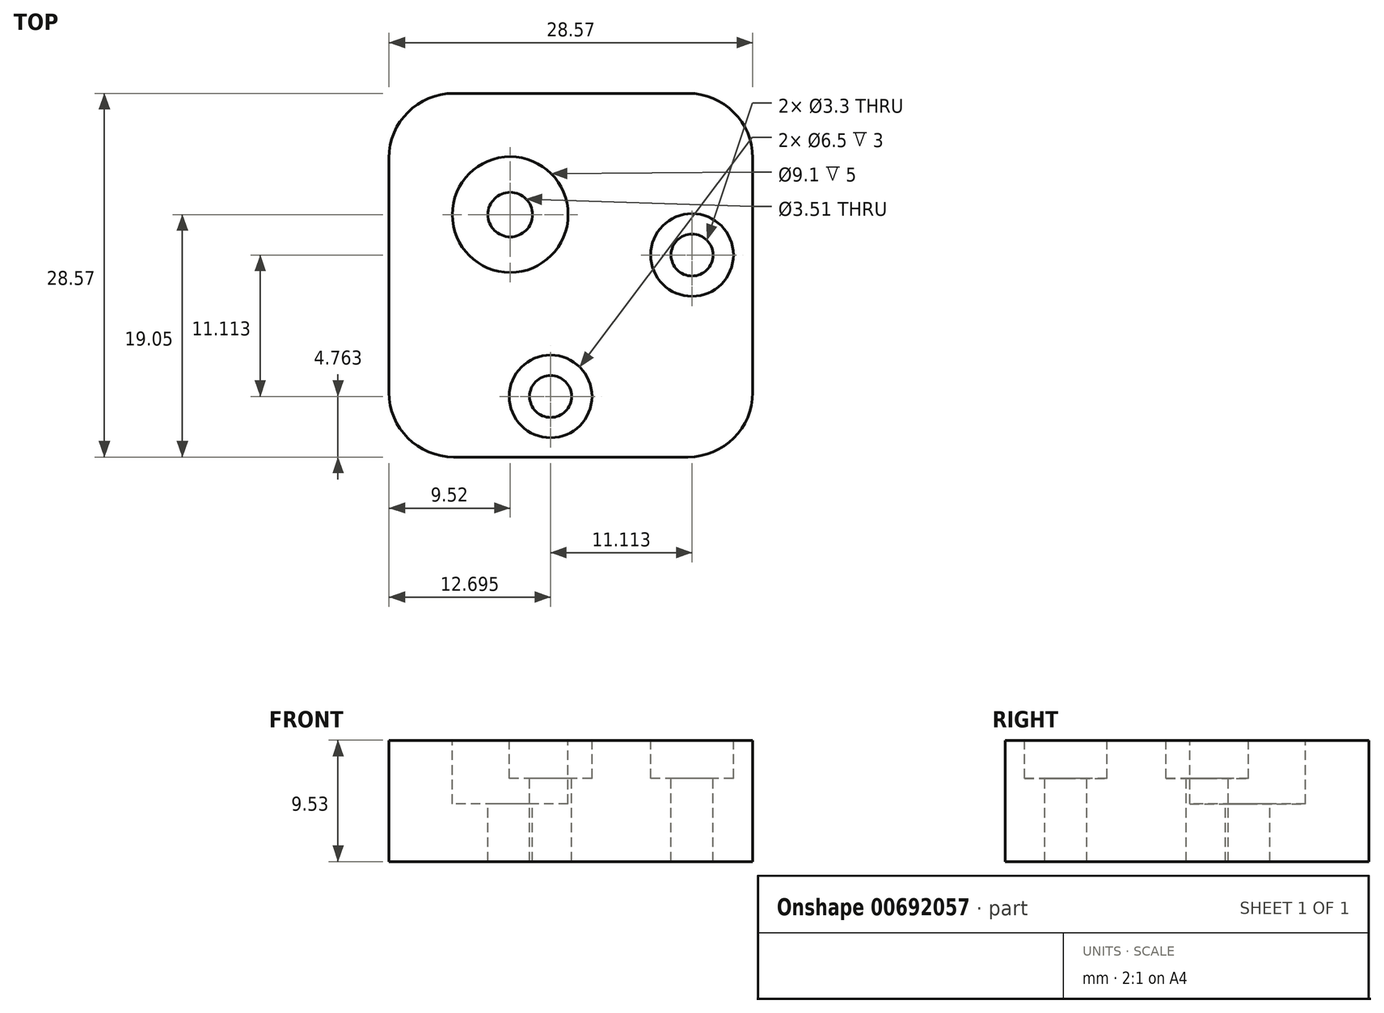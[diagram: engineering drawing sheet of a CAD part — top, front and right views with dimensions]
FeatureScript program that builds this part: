
annotation { "Feature Type Name" : "Feature", "Feature Type Description" : "" }
export const myFeature = defineFeature(function(context is Context, id is Id, definition is map)
    precondition{}
    {
        {
            var Q0;
            Q0=qCreatedBy(makeId("Top.planeOp"),FACE);
            var sketch = newSketch(context, id + "F0", { "sketchPlane" : qUnion([Q0])});
            skLineSegment(sketch, "E0.bottom", {"start": v(0, 0) * mm, "end": v(-28.58, 0) * mm});
            skLineSegment(sketch, "E0.top", {"start": v(0, 28.58) * mm, "end": v(-28.58, 28.58) * mm});
            skLineSegment(sketch, "E0.left", {"start": v(0, 0) * mm, "end": v(0, 28.58) * mm});
            skLineSegment(sketch, "E0.right", {"start": v(-28.58, 0) * mm, "end": v(-28.58, 28.58) * mm});
            skSolve(sketch);
        }
        {
            var Q0;
            Q0=makeQuery(id+"F0.imprint","IMPRINT",FACE,{"disambiguationData":[TD([[makeQuery(id+"F0.imprint","IMPRINT",EDGE,{"derivedFrom":sQuery(id+"F0.wireOp",EDGE,"E0.bottom")}),-1.0]])]});
            extrude(context, id + "F1", {"entities" : qUnion([Q0]), "depth" : 9.52 * mm, "offsetDistance" : 25.4 * mm});
        }
        {
            var Q0;
            Q0=makeQuery(id+"F1.opExtrude","CAP_FACE",FACE,{"disambiguationData":[OSD([sQuery(id+"F0.wireOp",EDGE,"E0.bottom"),sQuery(id+"F0.wireOp",EDGE,"E0.top"),sQuery(id+"F0.wireOp",EDGE,"E0.left"),sQuery(id+"F0.wireOp",EDGE,"E0.right")])],"isStart":false});
            var sketch = newSketch(context, id + "F2", { "sketchPlane" : qUnion([Q0])});
            skPoint(sketch, "E1", {"position": v(-4.76, 15.88) * mm});
            skPoint(sketch, "E2", {"position": v(-15.88, 4.76) * mm});
            skSolve(sketch);
        }
        {
            var Q0;
            Q0=sQuery(id+"F2.wireOp",VERTEX,"E2");
            var Q1;
            Q1=sQuery(id+"F2.wireOp",VERTEX,"E1");
            var Q2;
            Q2=makeQuery(id+"F1.opExtrude","SWEPT_BODY",BODY,{"disambiguationData":[OSD([sQuery(id+"F0.wireOp",EDGE,"E0.bottom"),sQuery(id+"F0.wireOp",EDGE,"E0.top"),sQuery(id+"F0.wireOp",EDGE,"E0.left"),sQuery(id+"F0.wireOp",EDGE,"E0.right")])]});
            hole(context, id + "F3", {"style" : HoleStyle.C_BORE, "endStyle" : HoleEndStyle.THROUGH, "standardTappedOrClearance" : lookupTablePath({ "standard" : "ISO", "fit" : "Normal", "size" : "M3", "type" : "Clearance" }), "standardBlindInLast" : lookupTablePath({ "fit" : "Standard", "standard" : "ISO", "size" : "M3", "type" : "Clearance" }), "holeDiameter" : 3.3 * mm, "cBoreDiameter" : 6.5 * mm, "cBoreDepth" : 3 * mm, "majorDiameter" : 6.35 * mm, "isTappedThrough" : true, "tappedDepth" : 12.7 * mm, "tapClearance" : 3, "locations" : qUnion([Q0, Q1]), "scope" : qUnion([Q2])});
        }
        {
            var Q0;
            Q0=makeQuery(id+"F1.opExtrude","CAP_FACE",FACE,{"disambiguationData":[OSD([sQuery(id+"F0.wireOp",EDGE,"E0.bottom"),sQuery(id+"F0.wireOp",EDGE,"E0.top"),sQuery(id+"F0.wireOp",EDGE,"E0.left"),sQuery(id+"F0.wireOp",EDGE,"E0.right")])],"isStart":false});
            var sketch = newSketch(context, id + "F4", { "sketchPlane" : qUnion([Q0])});
            skCircle(sketch, "E3", {"center": v(-19.05, 19.05) * mm, "radius": 4.55 * mm});
            skSolve(sketch);
        }
        {
            var Q0;
            Q0=makeQuery(id+"F4.imprint","IMPRINT",FACE,{"disambiguationData":[TD([[makeQuery(id+"F4.imprint","IMPRINT",EDGE,{"derivedFrom":sQuery(id+"F4.wireOp",EDGE,"E3")}),1.0]])]});
            extrude(context, id + "F5", {"entities" : qUnion([Q0]), "operationType" : NewBodyOperationType.REMOVE, "oppositeDirection" : true, "depth" : 5 * mm, "offsetDistance" : 25.4 * mm});
        }
        {
            var Q0;
            Q0=makeQuery(id+"F5.boolean.opBoolean","COPY",FACE,{"derivedFrom":makeQuery(id+"F5.opExtrude","CAP_FACE",FACE,{"disambiguationData":[OSD([sQuery(id+"F4.wireOp",EDGE,"E3")])],"isStart":false})});
            var sketch = newSketch(context, id + "F6", { "sketchPlane" : qUnion([Q0])});
            skCircle(sketch, "E4", {"center": v(-19.05, 19.05) * mm, "radius": 1.75 * mm});
            skSolve(sketch);
        }
        {
            var Q0;
            Q0=makeQuery(id+"F6.imprint","IMPRINT",FACE,{"disambiguationData":[TD([[makeQuery(id+"F6.imprint","IMPRINT",EDGE,{"derivedFrom":sQuery(id+"F6.wireOp",EDGE,"E4")}),1.0]])]});
            extrude(context, id + "F7", {"entities" : qUnion([Q0]), "operationType" : NewBodyOperationType.REMOVE, "endBound" : BoundingType.THROUGH_ALL, "oppositeDirection" : true, "depth" : 25.4 * mm, "offsetDistance" : 25.4 * mm});
        }
        {
            var Q0;
            Q0=makeQuery(id+"F1.opExtrude","SWEPT_EDGE",EDGE,{"disambiguationData":[OSD([sQuery(id+"F0.wireOp",EDGE,"E0.bottom"),sQuery(id+"F0.wireOp",EDGE,"E0.left")])]});
            var Q1;
            Q1=makeQuery(id+"F1.opExtrude","SWEPT_EDGE",EDGE,{"disambiguationData":[OSD([sQuery(id+"F0.wireOp",EDGE,"E0.bottom"),sQuery(id+"F0.wireOp",EDGE,"E0.right")])]});
            var Q2;
            Q2=makeQuery(id+"F1.opExtrude","SWEPT_EDGE",EDGE,{"disambiguationData":[OSD([sQuery(id+"F0.wireOp",EDGE,"E0.top"),sQuery(id+"F0.wireOp",EDGE,"E0.right")])]});
            var Q3;
            Q3=makeQuery(id+"F1.opExtrude","SWEPT_EDGE",EDGE,{"disambiguationData":[OSD([sQuery(id+"F0.wireOp",EDGE,"E0.top"),sQuery(id+"F0.wireOp",EDGE,"E0.left")])]});
            fillet(context, id + "F8", {"entities" : qUnion([Q0, Q1, Q2, Q3]), "radius" : 5.08 * mm, "tangentPropagation" : true, "allowEdgeOverflow" : false});
        }
    });
